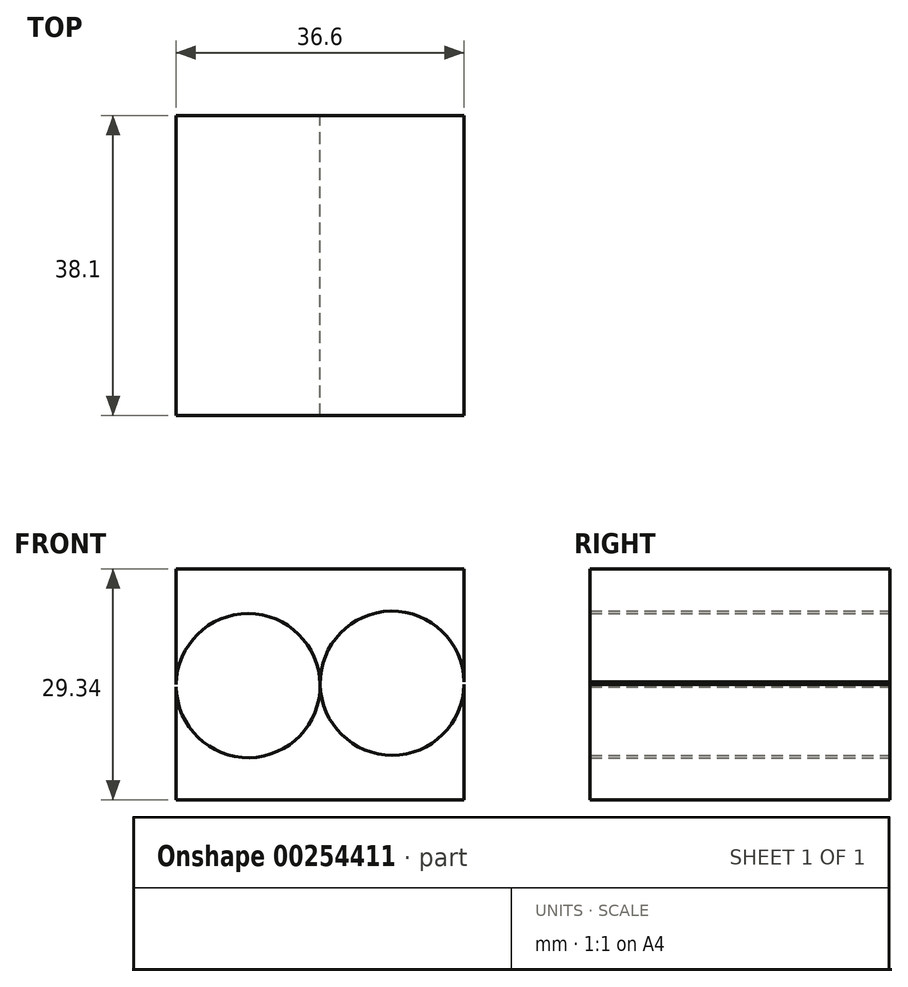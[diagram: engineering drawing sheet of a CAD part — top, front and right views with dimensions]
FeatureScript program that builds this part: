
annotation { "Feature Type Name" : "Feature", "Feature Type Description" : "" }
export const myFeature = defineFeature(function(context is Context, id is Id, definition is map)
    precondition{}
    {
        {
            var Q0;
            Q0=qCreatedBy(makeId("Front.planeOp"),FACE);
            var sketch = newSketch(context, id + "F0", { "sketchPlane" : qUnion([Q0])});
            skLineSegment(sketch, "E0.bottom", {"start": v(-5.52, 0) * mm, "end": v(5.52, 0) * mm});
            skLineSegment(sketch, "E0.top", {"start": v(-5.52, 0) * mm, "end": v(5.52, 0) * mm});
            skLineSegment(sketch, "E0.left", {"start": v(-5.52, 0) * mm, "end": v(-5.52, 0) * mm});
            skLineSegment(sketch, "E0.right", {"start": v(5.52, 0) * mm, "end": v(5.52, 0) * mm});
            skPoint(sketch, "E0.middle", {"position": v(0, 0) * mm});
            skLineSegment(sketch, "E1.bottom", {"start": v(-18.3, -14.67) * mm, "end": v(18.3, -14.67) * mm});
            skLineSegment(sketch, "E1.top", {"start": v(-18.3, 14.67) * mm, "end": v(18.3, 14.67) * mm});
            skLineSegment(sketch, "E1.left", {"start": v(-18.3, -14.67) * mm, "end": v(-18.3, 14.67) * mm});
            skLineSegment(sketch, "E1.right", {"start": v(18.3, -14.67) * mm, "end": v(18.3, 14.67) * mm});
            skCircle(sketch, "E2", {"center": v(-9.15, -0.15) * mm, "radius": 9.15 * mm});
            skPoint(sketch, "E2.second.point", {"position": v(-18.3, 0) * mm});
            skPoint(sketch, "E2.third.point", {"position": v(-15.97, -6.24) * mm});
            skCircle(sketch, "E3", {"center": v(9.15, 0.16) * mm, "radius": 9.15 * mm});
            skPoint(sketch, "E3.second.point", {"position": v(18.3, 0) * mm});
            skPoint(sketch, "E3.third.point", {"position": v(2.61, -6.24) * mm});
            skSolve(sketch);
        }
        {
            var Q0;
            {var subQ0=sQuery(id+"F0.wireOp",EDGE,"E2");var subQ1=sQuery(id+"F0.wireOp",EDGE,"E1.left");var subQ2=makeQuery(id+"F0.imprint","INTERSECT",VERTEX,{"disambiguationData":[OD(0.0)],"derivedFrom":[subQ1,subQ0]});Q0=makeQuery(id+"F0.imprint","IMPRINT",FACE,{"disambiguationData":[TD([[makeQuery(id+"F0.imprint","IMPRINT",EDGE,{"disambiguationData":[TD([[subQ2,-1.0]])],"derivedFrom":subQ1}),1.0]])]});}
            var Q1;
            {var subQ0=sQuery(id+"F0.wireOp",EDGE,"E3");var subQ1=sQuery(id+"F0.wireOp",EDGE,"E1.right");var subQ2=makeQuery(id+"F0.imprint","INTERSECT",VERTEX,{"disambiguationData":[OD(0.0)],"derivedFrom":[subQ1,subQ0]});Q1=makeQuery(id+"F0.imprint","IMPRINT",FACE,{"disambiguationData":[TD([[makeQuery(id+"F0.imprint","IMPRINT",EDGE,{"disambiguationData":[TD([[subQ2,-1.0]])],"derivedFrom":subQ1}),-1.0]])]});}
            var Q2;
            {var subQ6=sQuery(id+"F0.wireOp",EDGE,"E1.bottom");Q2=makeQuery(id+"F0.imprint","IMPRINT",FACE,{"disambiguationData":[TD([[makeQuery(id+"F0.imprint","IMPRINT",EDGE,{"derivedFrom":subQ6}),1.0]])]});}
            var Q3;
            {var subQ5=sQuery(id+"F0.wireOp",EDGE,"E1.top");Q3=makeQuery(id+"F0.imprint","IMPRINT",FACE,{"disambiguationData":[TD([[makeQuery(id+"F0.imprint","IMPRINT",EDGE,{"derivedFrom":subQ5}),-1.0]])]});}
            extrude(context, id + "F1", {"entities" : qUnion([Q0, Q1, Q2, Q3]), "depth" : 38.1 * mm});
        }
    });
